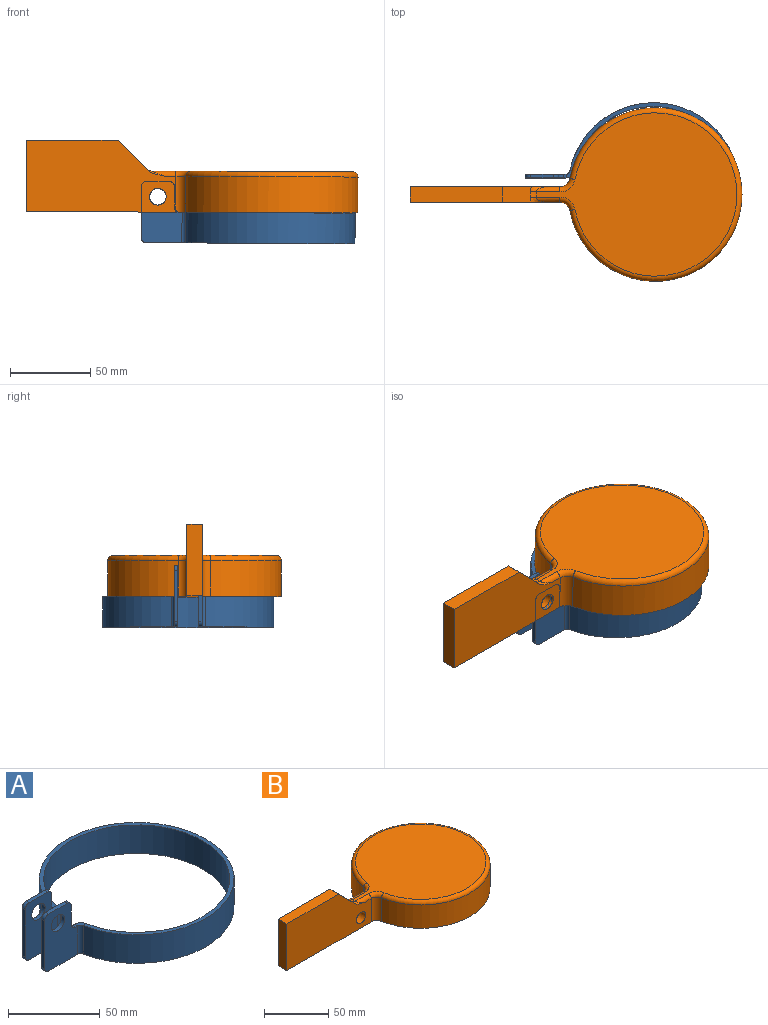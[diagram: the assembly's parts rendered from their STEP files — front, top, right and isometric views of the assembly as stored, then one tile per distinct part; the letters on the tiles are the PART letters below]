
ASSEMBLY  parts=2 mates=1
PART A: 36 faces, bbox 133x106.4x38.1 mm
  f0: plane 106.38x105.3mm, normal (0,0,-1), area 730mm2, adj f2,f3,f16,f32
  f1: plane 106.38x105.3mm, normal (0,0,1), area 730mm2, adj f2,f3,f17,f33
  f2: cylinder r=50.8mm len=101.6mm, axis (0,0,1), area 5690.4mm2, adj f0,f1,f18,f34
  f3: cylinder r=53.19mm len=106.38mm, axis (0,0,1), area 5957.9mm2, adj f0,f1,f19,f35
  f4: cylinder r=3.17mm len=3.18mm, axis (0,-1,0), area 11.9mm2, adj f5,f10,f11,f12
  f5: plane 12.7x2.39mm, normal (1,0,0), area 30.3mm2, adj f4,f11,f12,f15
  f6: plane 14.28x2.39mm, normal (0,0,1), area 34.1mm2, adj f11,f12,f13,f15
  f7: plane 31.75x2.39mm, normal (-1,0,0), area 75.8mm2, adj f11,f12,f13,f14
  f8: plane 22.23x2.39mm, normal (0,0,-1), area 53.1mm2, adj f11,f12,f14,f16
  f9: cylinder r=5.16mm len=10.31mm, axis (0,-1,0), area 77.4mm2, adj f11,f12
  f10: plane 2.39x1.6mm, normal (0,0,1), area 3.8mm2, adj f4,f11,f12,f17
  f11: plane 38.1x25.4mm, normal (0,-1,0), area 788.9mm2, adj f4,f5,f6,f7,f8,f9,f10,f13
  f12: plane 38.1x25.4mm, normal (0,1,0), area 788.9mm2, adj f4,f5,f6,f7,f8,f9,f10,f13
  f13: cylinder r=3.17mm len=3.18mm, axis (0,1,0), area 11.9mm2, adj f6,f7,f11,f12
  f14: cylinder r=3.17mm len=3.18mm, axis (0,-1,0), area 11.9mm2, adj f7,f8,f11,f12
  f15: cylinder r=3.17mm len=3.18mm, axis (0,-1,0), area 11.9mm2, adj f5,f6,f11,f12
  f16: plane 4.68x4.3mm, normal (0,0,-1), area 11.7mm2, adj f0,f8,f18,f19
  f17: plane 4.68x4.3mm, normal (0,0,1), area 11.7mm2, adj f1,f10,f18,f19
  f18: cylinder r=4.78mm len=19.05mm, axis (0,0,1), area 124.6mm2, adj f2,f11,f16,f17
  f19: cylinder r=2.39mm len=19.05mm, axis (0,0,1), area 62.3mm2, adj f3,f12,f16,f17
  f20: cylinder r=3.17mm len=3.18mm, axis (0,1,0), area 11.9mm2, adj f21,f26,f27,f28
  f21: plane 2.39x1.6mm, normal (0,0,1), area 3.8mm2, adj f20,f27,f28,f33
  f22: plane 22.23x2.39mm, normal (0,0,-1), area 53.1mm2, adj f27,f28,f30,f32
  f23: plane 31.75x2.39mm, normal (-1,0,0), area 75.8mm2, adj f27,f28,f29,f30
  f24: plane 14.28x2.39mm, normal (0,0,1), area 34.1mm2, adj f27,f28,f29,f31
  f25: cylinder r=5.16mm len=10.31mm, axis (0,1,0), area 77.4mm2, adj f27,f28
  f26: plane 12.7x2.39mm, normal (1,0,0), area 30.3mm2, adj f20,f27,f28,f31
  f27: plane 38.1x25.4mm, normal (0,1,0), area 788.9mm2, adj f20,f21,f22,f23,f24,f25,f26,f29
  f28: plane 38.1x25.4mm, normal (0,-1,0), area 788.9mm2, adj f20,f21,f22,f23,f24,f25,f26,f29
  f29: cylinder r=3.17mm len=3.18mm, axis (0,-1,0), area 11.9mm2, adj f23,f24,f27,f28
  f30: cylinder r=3.17mm len=3.18mm, axis (0,1,0), area 11.9mm2, adj f22,f23,f27,f28
  f31: cylinder r=3.17mm len=3.18mm, axis (0,-1,0), area 11.9mm2, adj f24,f26,f27,f28
  f32: plane 4.68x4.3mm, normal (0,0,-1), area 11.7mm2, adj f0,f22,f34,f35
  f33: plane 4.68x4.3mm, normal (0,0,1), area 11.7mm2, adj f1,f21,f34,f35
  f34: cylinder r=4.78mm len=19.05mm, axis (0,0,1), area 124.6mm2, adj f2,f27,f32,f33
  f35: cylinder r=2.39mm len=19.05mm, axis (0,0,1), area 62.3mm2, adj f3,f28,f32,f33
PART B: 19 faces, bbox 214x120x47.6 mm
  f0: cylinder r=6.35mm len=22.23mm, axis (0,0,-1), area 195.5mm2, adj f1,f4,f7,f13
  f1: plane 96.25x47.59mm, normal (0,1,0), area 3511.2mm2, adj f0,f5,f6,f7,f9,f14,f17,f18
  f2: plane 96.25x47.59mm, normal (0,-1,0), area 3511.2mm2, adj f3,f5,f6,f7,f9,f10,f15,f18
  f3: cylinder r=6.35mm len=22.23mm, axis (0,0,-1), area 195.5mm2, adj f2,f4,f7,f11
  f4: cylinder r=53.98mm len=107.95mm, axis (0,0,-1), area 7092.8mm2, adj f0,f3,f7,f12
  f5: plane 44.45x9.53mm, normal (-1,0,0), area 423.4mm2, adj f1,f2,f6,f7
  f6: plane 57.15x9.53mm, normal (0,0,1), area 544.4mm2, adj f1,f2,f5,f9
  f7: plane 206.38x107.95mm, normal (0,0,-1), area 10102.5mm2, adj f0,f1,f2,f3,f4,f5
  f8: plane 124.9x101.6mm, normal (0,0,1), area 8209.4mm2, adj f10,f11,f12,f13,f14,f16
  f9: plane 18.2x18.2mm, normal (0.71,0,0.71), area 238.4mm2, adj f1,f2,f6,f15,f16,f17
  f10: cylinder r=3.17mm len=14.8mm, axis (-1,0,0), area 53.2mm2, adj f2,f8,f11,f15
  f11: torus R=9.53mm, axis (0,0,1), area 51.9mm2, adj f3,f8,f10,f12
  f12: torus R=50.8mm, axis (0,0,1), area 1557.6mm2, adj f4,f8,f11,f13
  f13: torus R=9.53mm, axis (0,0,1), area 51.9mm2, adj f0,f8,f12,f14
  f14: cylinder r=3.17mm len=14.8mm, axis (1,0,0), area 53.2mm2, adj f1,f8,f13,f17
  f15: bspline ~11.85x8.26mm, area 32.1mm2, adj f2,f9,f10,f16
  f16: cylinder r=5.08mm len=3.59mm, axis (0,1,0), area 12.7mm2, adj f8,f9,f15,f17
  f17: bspline ~11.85x8.26mm, area 32.1mm2, adj f1,f9,f14,f16
  f18: cylinder r=5.16mm len=10.31mm, axis (0,-1,0), area 308.6mm2, adj f1,f2
PLACE A rot(axis=(0,1,0),0.3deg) t=(0.98,3.98,-15.75)mm fixed
PLACE B rot(axis=(0,1,0),0.2deg) t=(2,0,3.46)mm
MATE revolute B.f18 <-> A.f25  axis (0,-1,0) through (-68.39,-4.76,13.24)mm
